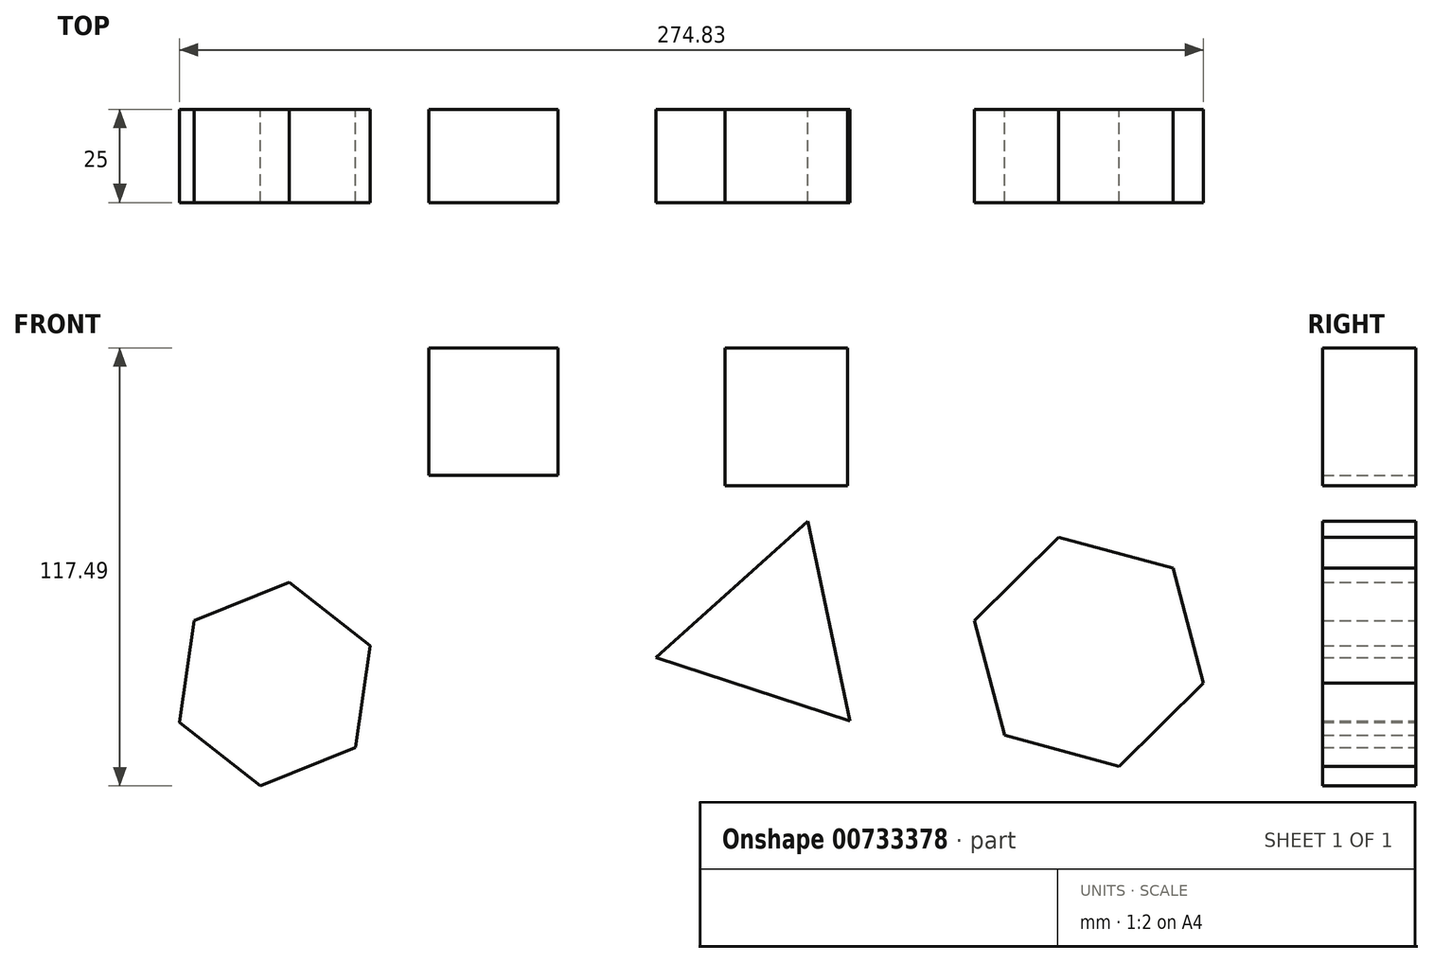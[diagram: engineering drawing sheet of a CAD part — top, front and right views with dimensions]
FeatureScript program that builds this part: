
annotation { "Feature Type Name" : "Feature", "Feature Type Description" : "" }
export const myFeature = defineFeature(function(context is Context, id is Id, definition is map)
    precondition{}
    {
        {
            var Q0;
            Q0=qCreatedBy(makeId("Front.planeOp"),FACE);
            var sketch = newSketch(context, id + "F0", { "sketchPlane" : qUnion([Q0])});
            skLineSegment(sketch, "E0.bottom", {"start": v(-64.6, 25.87) * mm, "end": v(-29.92, 25.87) * mm});
            skLineSegment(sketch, "E0.top", {"start": v(-64.6, 59.98) * mm, "end": v(-29.92, 59.98) * mm});
            skLineSegment(sketch, "E0.left", {"start": v(-64.6, 25.87) * mm, "end": v(-64.6, 59.98) * mm});
            skLineSegment(sketch, "E0.right", {"start": v(-29.92, 25.87) * mm, "end": v(-29.92, 59.98) * mm});
            skPoint(sketch, "E0.middle", {"position": v(-47.26, 42.93) * mm});
            skLineSegment(sketch, "E1.bottom", {"start": v(14.89, 22.98) * mm, "end": v(47.84, 22.98) * mm});
            skLineSegment(sketch, "E1.top", {"start": v(14.89, 59.98) * mm, "end": v(47.84, 59.98) * mm});
            skLineSegment(sketch, "E1.left", {"start": v(14.89, 22.98) * mm, "end": v(14.89, 59.98) * mm});
            skLineSegment(sketch, "E1.right", {"start": v(47.84, 22.98) * mm, "end": v(47.84, 59.98) * mm});
            skPoint(sketch, "E1.middle", {"position": v(31.36, 41.48) * mm});
            skSolve(sketch);
        }
        {
            var Q0;
            Q0=makeQuery(id+"F0.imprint","IMPRINT",FACE,{"disambiguationData":[TD([[makeQuery(id+"F0.imprint","IMPRINT",EDGE,{"derivedFrom":sQuery(id+"F0.wireOp",EDGE,"E0.bottom")}),1.0]])]});
            var Q1;
            Q1=makeQuery(id+"F0.imprint","IMPRINT",FACE,{"disambiguationData":[TD([[makeQuery(id+"F0.imprint","IMPRINT",EDGE,{"derivedFrom":sQuery(id+"F0.wireOp",EDGE,"E1.bottom")}),1.0]])]});
            extrude(context, id + "F1", {"entities" : qUnion([Q0, Q1]), "depth" : 25 * mm, "offsetDistance" : 25 * mm});
        }
        {
            var Q0;
            Q0=qCreatedBy(makeId("Front.planeOp"),FACE);
            var sketch = newSketch(context, id + "F2", { "sketchPlane" : qUnion([Q0])});
            skCircle(sketch, "E2.cCircle", {"center": v(-105.94, -30.2) * mm, "radius": 23.88 * mm, "construction": true});
            skLineSegment(sketch, "E2.0", {"start": v(-109.84, -57.5) * mm, "end": v(-131.53, -40.49) * mm});
            skLineSegment(sketch, "E2.1", {"start": v(-131.53, -40.49) * mm, "end": v(-127.64, -13.18) * mm});
            skLineSegment(sketch, "E2.2", {"start": v(-127.64, -13.18) * mm, "end": v(-102.05, -2.9) * mm});
            skLineSegment(sketch, "E2.3", {"start": v(-102.05, -2.9) * mm, "end": v(-80.35, -19.93) * mm});
            skLineSegment(sketch, "E2.4", {"start": v(-80.35, -19.93) * mm, "end": v(-84.25, -47.23) * mm});
            skLineSegment(sketch, "E2.5", {"start": v(-84.25, -47.23) * mm, "end": v(-109.84, -57.5) * mm});
            skPoint(sketch, "E2.0.midPoint", {"position": v(-120.69, -49) * mm});
            skSolve(sketch);
        }
        {
            var Q0;
            Q0=makeQuery(id+"F2.imprint","IMPRINT",FACE,{"disambiguationData":[TD([[makeQuery(id+"F2.imprint","IMPRINT",EDGE,{"derivedFrom":sQuery(id+"F2.wireOp",EDGE,"E2.0")}),-1.0]])]});
            extrude(context, id + "F3", {"entities" : qUnion([Q0]), "depth" : 25 * mm, "offsetDistance" : 25 * mm});
        }
        {
            var Q0;
            Q0=qCreatedBy(makeId("Front.planeOp"),FACE);
            var sketch = newSketch(context, id + "F4", { "sketchPlane" : qUnion([Q0])});
            skCircle(sketch, "E3.cCircle", {"center": v(27.32, -16.62) * mm, "radius": 15.81 * mm, "construction": true});
            skLineSegment(sketch, "E3.0", {"start": v(48.44, -40.16) * mm, "end": v(-3.63, -23.14) * mm});
            skLineSegment(sketch, "E3.1", {"start": v(-3.63, -23.14) * mm, "end": v(37.15, 13.44) * mm});
            skLineSegment(sketch, "E3.2", {"start": v(37.15, 13.44) * mm, "end": v(48.44, -40.16) * mm});
            skPoint(sketch, "E3.0.midPoint", {"position": v(22.4, -31.65) * mm});
            skCircle(sketch, "E4.cCircle", {"center": v(112.6, -21.54) * mm, "radius": 27.56 * mm, "construction": true});
            skLineSegment(sketch, "E4.0", {"start": v(120.72, -52.3) * mm, "end": v(90.01, -43.96) * mm});
            skLineSegment(sketch, "E4.1", {"start": v(90.01, -43.96) * mm, "end": v(81.88, -13.2) * mm});
            skLineSegment(sketch, "E4.2", {"start": v(81.88, -13.2) * mm, "end": v(104.46, 9.23) * mm});
            skLineSegment(sketch, "E4.3", {"start": v(104.46, 9.23) * mm, "end": v(135.17, 0.89) * mm});
            skLineSegment(sketch, "E4.4", {"start": v(135.17, 0.89) * mm, "end": v(143.3, -29.88) * mm});
            skLineSegment(sketch, "E4.5", {"start": v(143.3, -29.88) * mm, "end": v(120.72, -52.3) * mm});
            skPoint(sketch, "E4.0.midPoint", {"position": v(105.37, -48.13) * mm});
            skSolve(sketch);
        }
        {
            var Q0;
            Q0=makeQuery(id+"F4.imprint","IMPRINT",FACE,{"disambiguationData":[TD([[makeQuery(id+"F4.imprint","IMPRINT",EDGE,{"derivedFrom":sQuery(id+"F4.wireOp",EDGE,"E3.0")}),-1.0]])]});
            var Q1;
            Q1=makeQuery(id+"F4.imprint","IMPRINT",FACE,{"disambiguationData":[TD([[makeQuery(id+"F4.imprint","IMPRINT",EDGE,{"derivedFrom":sQuery(id+"F4.wireOp",EDGE,"E4.0")}),-1.0]])]});
            extrude(context, id + "F5", {"entities" : qUnion([Q0, Q1]), "depth" : 25 * mm, "offsetDistance" : 25 * mm});
        }
    });
